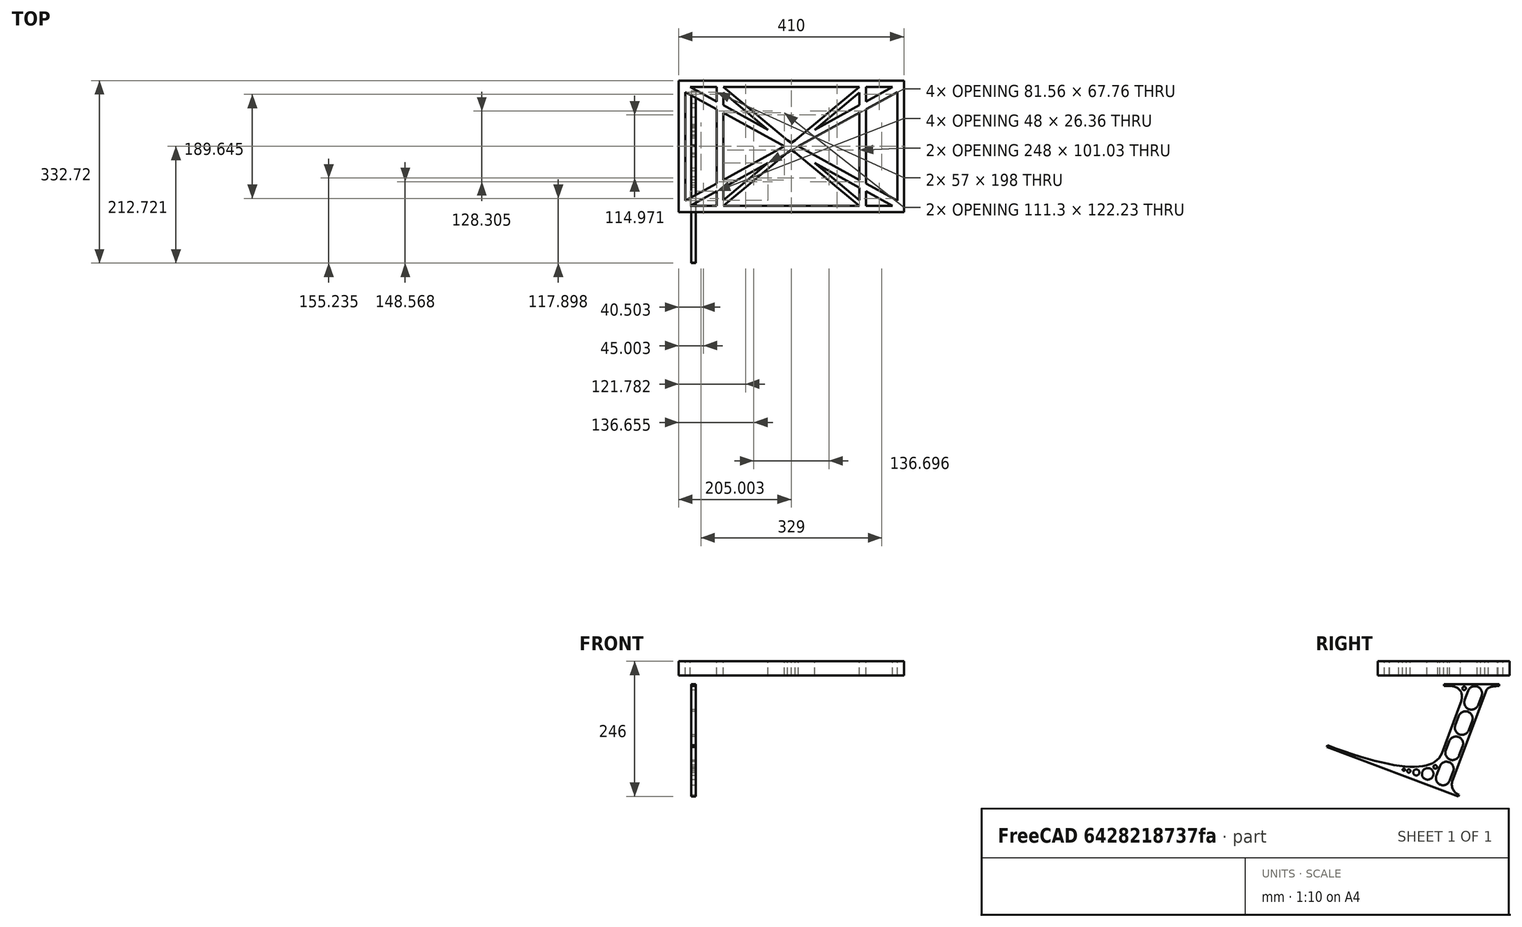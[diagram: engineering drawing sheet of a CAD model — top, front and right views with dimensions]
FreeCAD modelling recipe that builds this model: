
FCSTD DOCUMENT  (FreeCAD 0.19R0.19.2)
Label: laptopStand037
License: All rights reserved
LicenseURL: http://en.wikipedia.org/wiki/All_rights_reserved
objects: Sketcher::SketchObject×3, Part::Extrusion×2
note: 5 computed .brp shape members not serialized (recipe doc carries the construction recipe); baked Part::Feature solids carry a one-line shape summary decoded from their .brp

FEATURE [Sketcher::SketchObject] Sketch
  FullyConstrained = true
  sketch-geometry (52):
    g0: LineSegment StartX=-22.9272 StartY=136.221 StartZ=0 EndX=-22.9272 EndY=-103.779 EndZ=0
    g1: LineSegment StartX=-22.9272 StartY=136.221 StartZ=0 EndX=387.073 EndY=136.221 EndZ=0
    g2: LineSegment StartX=-22.9272 StartY=-103.779 StartZ=0 EndX=387.073 EndY=-103.779 EndZ=0
    g3: LineSegment StartX=387.073 StartY=136.221 StartZ=0 EndX=387.073 EndY=-103.779 EndZ=0
    g4: LineSegment StartX=375.073 StartY=115.221 StartZ=0 EndX=318.073 EndY=83.9235 EndZ=0
    g5: LineSegment StartX=-10.9272 StartY=-82.7794 StartZ=0 EndX=46.0728 EndY=-51.4823 EndZ=0
    g6: LineSegment StartX=-1.92719 StartY=124.221 StartZ=0 EndX=46.0728 EndY=97.8651 EndZ=0
    g7: LineSegment StartX=366.073 StartY=-91.7794 StartZ=0 EndX=318.073 EndY=-65.424 EndZ=0
    g8: LineSegment StartX=-10.9272 StartY=115.221 StartZ=0 EndX=-10.9272 EndY=-82.7794 EndZ=0
    g9: LineSegment StartX=375.073 StartY=-82.7794 StartZ=0 EndX=375.073 EndY=115.221 EndZ=0
    g10: LineSegment StartX=-1.92719 StartY=-91.7794 StartZ=0 EndX=46.0728 EndY=-91.7794 EndZ=0
    g11: LineSegment StartX=318.073 StartY=124.221 StartZ=0 EndX=366.073 EndY=124.221 EndZ=0
    g12: LineSegment StartX=306.073 StartY=-81.8102 StartZ=0 EndX=224.513 EndY=-14.0532 EndZ=0
    g13: LineSegment StartX=58.0728 StartY=114.251 StartZ=0 EndX=139.632 EndY=46.4944 EndZ=0
    g14: LineSegment StartX=306.073 StartY=124.221 StartZ=0 EndX=189.124 EndY=27.0628 EndZ=0
    g15: LineSegment StartX=58.0728 StartY=-91.7794 StartZ=0 EndX=175.022 EndY=5.37834 EndZ=0
    g16: LineSegment StartX=46.0728 StartY=124.221 StartZ=0 EndX=46.0728 EndY=97.8651 EndZ=0
    g17: LineSegment StartX=58.0728 StartY=-81.8102 StartZ=0 EndX=58.0728 EndY=-58.8351 EndZ=0
    g18: LineSegment StartX=318.073 StartY=124.221 StartZ=0 EndX=318.073 EndY=97.8651 EndZ=0
    g19: LineSegment StartX=306.073 StartY=114.251 StartZ=0 EndX=306.073 EndY=91.2763 EndZ=0
    g20: LineSegment StartX=182.073 StartY=23.1914 StartZ=0 EndX=189.124 EndY=27.0628 EndZ=0
    g21: LineSegment StartX=182.073 StartY=9.24976 StartZ=0 EndX=175.022 EndY=5.37834 EndZ=0
    g22: LineSegment StartX=224.513 StartY=46.4944 StartZ=0 EndX=306.073 EndY=114.251 EndZ=0
    g23: LineSegment StartX=175.022 StartY=27.0628 StartZ=0 EndX=58.0728 EndY=124.221 EndZ=0
    g24: LineSegment StartX=169.377 StartY=16.2206 StartZ=0 EndX=58.0728 EndY=77.3346 EndZ=0
    g25: LineSegment StartX=139.632 StartY=-14.0532 StartZ=0 EndX=58.0728 EndY=-81.8102 EndZ=0
    g26: LineSegment StartX=194.768 StartY=16.2206 StartZ=0 EndX=306.073 EndY=-44.8935 EndZ=0
    g27: LineSegment StartX=224.513 StartY=46.4944 StartZ=0 EndX=306.073 EndY=91.2763 EndZ=0
    g28: LineSegment StartX=175.022 StartY=27.0628 StartZ=0 EndX=182.073 EndY=23.1914 EndZ=0
    g29: LineSegment StartX=139.632 StartY=-14.0532 StartZ=0 EndX=58.0728 EndY=-58.8351 EndZ=0
    g30: LineSegment StartX=189.124 StartY=5.37834 StartZ=0 EndX=182.073 EndY=9.24976 EndZ=0
    g31: LineSegment StartX=189.124 StartY=5.37834 StartZ=0 EndX=306.073 EndY=-91.7794 EndZ=0
    g32: LineSegment StartX=306.073 StartY=77.3346 StartZ=0 EndX=306.073 EndY=-44.8935 EndZ=0
    g33: LineSegment StartX=318.073 StartY=83.9235 StartZ=0 EndX=318.073 EndY=-51.4823 EndZ=0
    g34: LineSegment StartX=318.073 StartY=97.8651 StartZ=0 EndX=366.073 EndY=124.221 EndZ=0
    g35: LineSegment StartX=306.073 StartY=77.3346 StartZ=0 EndX=194.768 EndY=16.2206 EndZ=0
    g36: LineSegment StartX=306.073 StartY=-58.8351 StartZ=0 EndX=224.513 EndY=-14.0532 EndZ=0
    g37: LineSegment StartX=306.073 StartY=-58.8351 StartZ=0 EndX=306.073 EndY=-81.8102 EndZ=0
    g38: LineSegment StartX=318.073 StartY=-51.4823 StartZ=0 EndX=375.073 EndY=-82.7794 EndZ=0
    g39: LineSegment StartX=318.073 StartY=-65.424 StartZ=0 EndX=318.073 EndY=-91.7794 EndZ=0
    g40: LineSegment StartX=306.073 StartY=124.221 StartZ=0 EndX=58.0728 EndY=124.221 EndZ=0
    g41: LineSegment StartX=318.073 StartY=-91.7794 StartZ=0 EndX=366.073 EndY=-91.7794 EndZ=0
    g42: LineSegment StartX=58.0728 StartY=-91.7794 StartZ=0 EndX=306.073 EndY=-91.7794 EndZ=0
    g43: LineSegment StartX=58.0728 StartY=-44.8935 StartZ=0 EndX=58.0728 EndY=77.3346 EndZ=0
    g44: LineSegment StartX=46.0728 StartY=-65.424 StartZ=0 EndX=-1.92719 EndY=-91.7794 EndZ=0
    g45: LineSegment StartX=46.0728 StartY=-65.424 StartZ=0 EndX=46.0728 EndY=-91.7794 EndZ=0
    g46: LineSegment StartX=58.0728 StartY=-44.8935 StartZ=0 EndX=169.377 EndY=16.2206 EndZ=0
    g47: LineSegment StartX=58.0728 StartY=91.2763 StartZ=0 EndX=58.0728 EndY=114.251 EndZ=0
    g48: LineSegment StartX=46.0728 StartY=83.9235 StartZ=0 EndX=46.0728 EndY=-51.4823 EndZ=0
    g49: LineSegment StartX=46.0728 StartY=124.221 StartZ=0 EndX=-1.92719 EndY=124.221 EndZ=0
    g50: LineSegment StartX=58.0728 StartY=91.2763 StartZ=0 EndX=139.632 EndY=46.4944 EndZ=0
    g51: LineSegment StartX=46.0728 StartY=83.9235 StartZ=0 EndX=-10.9272 EndY=115.221 EndZ=0
  constraints (102):
    c: Vertical(g0)
    c: Distance(g0) = 240
    c: Horizontal(g1)
    c: Distance(g1) = 410
    c: Coincident(g1,g0)
    c: Coincident(g2,g0)
    c: Horizontal(g2)
    c: Coincident(g3,g1)
    c: Vertical(g3)
    c: Coincident(g2,g3)
    c: Block(g1)
    c: Horizontal(g10)
    c: Horizontal(g11)
    c: PointOnObject(g35,g6)
    c: Coincident(g28,g20)
    c: Coincident(g30,g21)
    c: Tangent(g7,g24)
    c: PointOnObject(g24,g5)
    c: PointOnObject(g26,g4)
    c: Coincident(g20,g14)
    c: Tangent(g20,g27)
    c: Coincident(g50,g13)
    c: Coincident(g28,g23)
    c: Coincident(g22,g27)
    c: Coincident(g21,g15)
    c: Coincident(g29,g25)
    c: Tangent(g21,g29)
    c: Coincident(g36,g12)
    c: Coincident(g31,g30)
    c: Coincident(g22,g19)
    c: Tangent(g19,g32)
    c: Tangent(g18,g33)
    c: Coincident(g27,g19)
    c: Tangent(g27,g34)
    c: Coincident(g4,g33)
    c: Coincident(g35,g32)
    c: Tangent(g4,g35)
    c: Coincident(g37,g12)
    c: Tangent(g7,g36)
    c: Tangent(g32,g37)
    c: Coincident(g26,g32)
    c: Tangent(g26,g38)
    c: Coincident(g33,g38)
    c: Coincident(g39,g7)
    c: Tangent(g33,g39)
    c: Coincident(g25,g17)
    c: Tangent(g17,g43)
    c: Coincident(g29,g17)
    c: Tangent(g29,g44)
    c: Coincident(g45,g44)
    c: Tangent(g16,g45)
    c: Coincident(g5,g48)
    c: Coincident(g46,g43)
    c: Tangent(g5,g46)
    c: Tangent(g43,g47)
    c: Tangent(g16,g48)
    c: Coincident(g13,g47)
    c: PointOnObject(g40,g23)
    c: Tangent(g40,g49)
    c: Coincident(g6,g16)
    c: Coincident(g50,g47)
    c: Tangent(g6,g50)
    c: Coincident(g24,g43)
    c: Coincident(g51,g48)
    c: Tangent(g24,g51)
    c: Block(g23)
    c: Block(g14)
    c: Block(g20)
    c: Block(g40)
    c: Block(g18)
    c: Block(g34)
    c: Block(g4)
    c: Block(g38)
    c: Block(g9)
    c: Block(g36)
    c: Block(g37)
    c: Block(g7)
    c: Block(g39)
    c: Block(g22)
    c: Block(g31)
    c: Block(g42)
    c: Block(g21)
    c: Block(g15)
    c: Block(g29)
    c: Block(g25)
    c: Block(g45)
    c: Block(g44)
    c: Block(g5)
    c: Block(g8)
    c: Block(g51)
    c: Block(g6)
    c: Block(g16)
    c: Block(g13)
    c: Block(g47)
    c: Block(g35)
    c: Block(g32)
    c: Block(g24)
    c: Block(g46)
    c: Block(g49)
    c: Block(g11)
    c: Block(g41)
    c: Block(g10)
FEATURE [Part::Extrusion] Extrude
  Base = -> Sketch
  Dir = (0,0,1)
  DirMode = 2
  FaceMakerClass = Part::FaceMakerBullseye
  LengthFwd = 26
  LengthRev = 0
  Solid = true
  Symmetric = false
FEATURE [Sketcher::SketchObject] Sketch001
  FullyConstrained = true
  MapMode = 4
  Placement = pos=(0,0,0) rot=(0.57735,0.57735,0.57735;2.0944rad)
  Support = -> [Sketch]
  sketch-geometry (46):
    g0: BSplineCurve PolesCount=3 KnotsCount=2 Degree=2 IsPeriodic=0
    g1: ArcOfCircle CenterX=73.122 CenterY=-32.2909 CenterZ=0 NormalX=0 NormalY=0 NormalZ=1 AngleXU=0 Radius=13 StartAngle=5.92268 EndAngle=9.06428
    g2: ArcOfCircle CenterX=66.7816 CenterY=-49.1439 CenterZ=0 NormalX=0 NormalY=0 NormalZ=1 AngleXU=0 Radius=13 StartAngle=2.78068 EndAngle=5.92131
    g3: ArcOfCircle CenterX=55.9263 CenterY=-78.1807 CenterZ=0 NormalX=0 NormalY=0 NormalZ=1 AngleXU=0 Radius=13 StartAngle=5.92268 EndAngle=9.06428
    g4: ArcOfCircle CenterX=49.5884 CenterY=-95.0342 CenterZ=0 NormalX=0 NormalY=0 NormalZ=1 AngleXU=0 Radius=13 StartAngle=2.78068 EndAngle=5.92131
    g5: ArcOfCircle CenterX=38.7206 CenterY=-124.067 CenterZ=0 NormalX=0 NormalY=0 NormalZ=1 AngleXU=0 Radius=13 StartAngle=5.92268 EndAngle=9.06428
    g6: ArcOfCircle CenterX=32.3875 CenterY=-140.92 CenterZ=0 NormalX=0 NormalY=0 NormalZ=1 AngleXU=0 Radius=13 StartAngle=2.78068 EndAngle=5.92131
    g7: ArcOfCircle CenterX=21.4715 CenterY=-169.934 CenterZ=0 NormalX=0 NormalY=0 NormalZ=1 AngleXU=0 Radius=13 StartAngle=5.92268 EndAngle=9.06428
    g8: ArcOfCircle CenterX=15.1336 CenterY=-186.787 CenterZ=0 NormalX=0 NormalY=0 NormalZ=1 AngleXU=0 Radius=13 StartAngle=2.78068 EndAngle=5.92131
    g9-g12: Circle x4 (B-spline internal-alignment scaffolding for g13; pole/knot coordinates omitted)
    g13: BSplineCurve PolesCount=4 KnotsCount=2 Degree=3 IsPeriodic=0
    g14: GeomPoint X=28.8094 Y=-19.0875 Z=0
    g15: GeomPoint X=47.0443 Y=-50.4712 Z=0
    g16: Circle CenterX=53.5586 CenterY=-23.2695 CenterZ=0 NormalX=0 NormalY=0 NormalZ=1 AngleXU=0 Radius=3.24518
    g17: Circle CenterX=-195.441 CenterY=-127.082 CenterZ=0 NormalX=0 NormalY=0 NormalZ=1 AngleXU=0 Radius=1
    g18: Circle CenterX=-8.24091 CenterY=-197.481 CenterZ=0 NormalX=0 NormalY=0 NormalZ=1 AngleXU=0 Radius=1
    g19: Circle CenterX=12.8789 CenterY=-141.321 CenterZ=0 NormalX=0 NormalY=0 NormalZ=1 AngleXU=0 Radius=1
    g20: BSplineCurve PolesCount=3 KnotsCount=2 Degree=2 IsPeriodic=0
    g21: GeomPoint X=-195.441 Y=-127.082 Z=0
    g22: GeomPoint X=12.8789 Y=-141.321 Z=0
    g23: Circle CenterX=-12.8016 CenterY=-179.036 CenterZ=0 NormalX=0 NormalY=0 NormalZ=1 AngleXU=0 Radius=10.5072
    g24: Circle CenterX=0.933922 CenterY=-166.43 CenterZ=0 NormalX=0 NormalY=0 NormalZ=1 AngleXU=0 Radius=3.26661
    g25: Circle CenterX=-33.5518 CenterY=-176.44 CenterZ=0 NormalX=0 NormalY=0 NormalZ=1 AngleXU=0 Radius=5.64388
    g26: Circle CenterX=-47.2366 CenterY=-173.859 CenterZ=0 NormalX=0 NormalY=0 NormalZ=1 AngleXU=0 Radius=3.01653
    g27: Circle CenterX=-56.2595 CenterY=-171.456 CenterZ=0 NormalX=0 NormalY=0 NormalZ=1 AngleXU=0 Radius=2.12826
    g28: ArcOfCircle CenterX=51.2151 CenterY=-198.473 CenterZ=0 NormalX=0 NormalY=0 NormalZ=1 AngleXU=0 Radius=20 StartAngle=2.78189 EndAngle=4.35269
    g29: LineSegment StartX=32.4951 StartY=-191.433 StartZ=0 EndX=94.6577 EndY=-26.1351 EndZ=0
    g30: LineSegment StartX=43.1192 StartY=-220.001 StartZ=0 EndX=-196.497 EndY=-129.89 EndZ=0
    g31: LineSegment StartX=43.1192 StartY=-220.001 StartZ=0 EndX=44.1752 EndY=-217.193 EndZ=0
    g32: LineSegment StartX=117.223 StartY=-19.0875 StartZ=0 EndX=117.223 EndY=-16.0875 EndZ=0
    g33: LineSegment StartX=117.223 StartY=-16.0875 StartZ=0 EndX=17.2232 EndY=-16.0875 EndZ=0
    g34: LineSegment StartX=17.2232 StartY=-16.0875 StartZ=0 EndX=17.2232 EndY=-19.0875 EndZ=0
    g35: LineSegment StartX=28.8094 StartY=-19.0875 StartZ=0 EndX=17.2232 EndY=-19.0875 EndZ=0
    g36: LineSegment StartX=47.0443 StartY=-50.4712 StartZ=0 EndX=12.8789 EndY=-141.321 EndZ=0
    g37: LineSegment StartX=-195.441 StartY=-127.082 StartZ=0 EndX=-196.497 EndY=-129.89 EndZ=0
    g38: LineSegment StartX=85.2864 StartY=-36.8765 StartZ=0 EndX=78.9396 EndY=-53.7463 EndZ=0
    g39: LineSegment StartX=60.9577 StartY=-27.7052 StartZ=0 EndX=54.6191 EndY=-44.5532 EndZ=0
    g40: LineSegment StartX=68.0907 StartY=-82.7664 StartZ=0 EndX=61.7465 EndY=-99.6365 EndZ=0
    g41: LineSegment StartX=43.7619 StartY=-73.595 StartZ=0 EndX=37.426 EndY=-90.4435 EndZ=0
    g42: LineSegment StartX=50.885 StartY=-128.652 StartZ=0 EndX=44.5456 EndY=-145.522 EndZ=0
    g43: LineSegment StartX=26.5562 StartY=-119.481 StartZ=0 EndX=20.2251 EndY=-136.329 EndZ=0
    g44: LineSegment StartX=9.3071 StartY=-165.349 StartZ=0 EndX=2.97115 EndY=-182.197 EndZ=0
    g45: LineSegment StartX=33.6358 StartY=-174.52 StartZ=0 EndX=27.2917 EndY=-191.39 EndZ=0
  constraints (70):
    c: Block(g0)
    c: Block(g1)
    c: Block(g2)
    c: Block(g4)
    c: Block(g3)
    c: Block(g6)
    c: Block(g5)
    c: Block(g8)
    c: Block(g7)
    c: Weight(g9) = 1
    c: Equal(g9,g10)
    c: Equal(g9,g11)
    c: Equal(g9,g12)
    c: InternalAlignment(g9-g12 -> g13) x4
    c: InternalAlignment(g14,g13)
    c: InternalAlignment(g15,g13)
    c: Block(g16)
    c: Weight(g17) = 1
    c: Equal(g17,g18)
    c: Equal(g17,g19)
    c: InternalAlignment(g17,g20)
    c: InternalAlignment(g18,g20)
    c: InternalAlignment(g19,g20)
    c: InternalAlignment(g21,g20)
    c: InternalAlignment(g22,g20)
    c: Block(g20)
    c: Block(g23)
    c: Block(g24)
    c: Block(g25)
    c: Block(g26)
    c: Block(g27)
    c: Block(g28)
    c: Coincident(g29,g28)
    c: Coincident(g29,g0)
    c: Block(g13)
    c: Coincident(g31,g30)
    c: Coincident(g31,g28)
    c: Block(g31)
    c: Coincident(g32,g0)
    c: Vertical(g32)
    c: Coincident(g33,g32)
    c: Horizontal(g33)
    c: Coincident(g34,g33)
    c: Vertical(g34)
    c: Block(g33)
    c: Coincident(g35,g13)
    c: Coincident(g35,g34)
    c: Horizontal(g35)
    c: Coincident(g36,g13)
    c: Coincident(g36,g20)
    c: Coincident(g37,g20)
    c: Coincident(g37,g30)
    c: Block(g30)
    c: Coincident(g38,g1)
    c: Coincident(g38,g2)
    c: Coincident(g39,g1)
    c: Coincident(g39,g2)
    c: Coincident(g40,g3)
    c: Coincident(g40,g4)
    c: Coincident(g41,g3)
    c: Coincident(g41,g4)
    c: Coincident(g42,g5)
    c: Coincident(g42,g6)
    c: Coincident(g43,g5)
    c: Coincident(g43,g6)
    c: Coincident(g44,g7)
    c: Coincident(g44,g8)
    c: Coincident(g45,g7)
    c: Coincident(g45,g8)
    c: Distance(g30) = 256
FEATURE [Part::Extrusion] Extrude002
  Base = -> Sketch001
  Dir = (1,0,0)
  DirMode = 2
  FaceMakerClass = Part::FaceMakerBullseye
  LengthFwd = 8
  LengthRev = 0
  Solid = true
  Symmetric = false
FEATURE [Sketcher::SketchObject] Sketch002
  FullyConstrained = true
